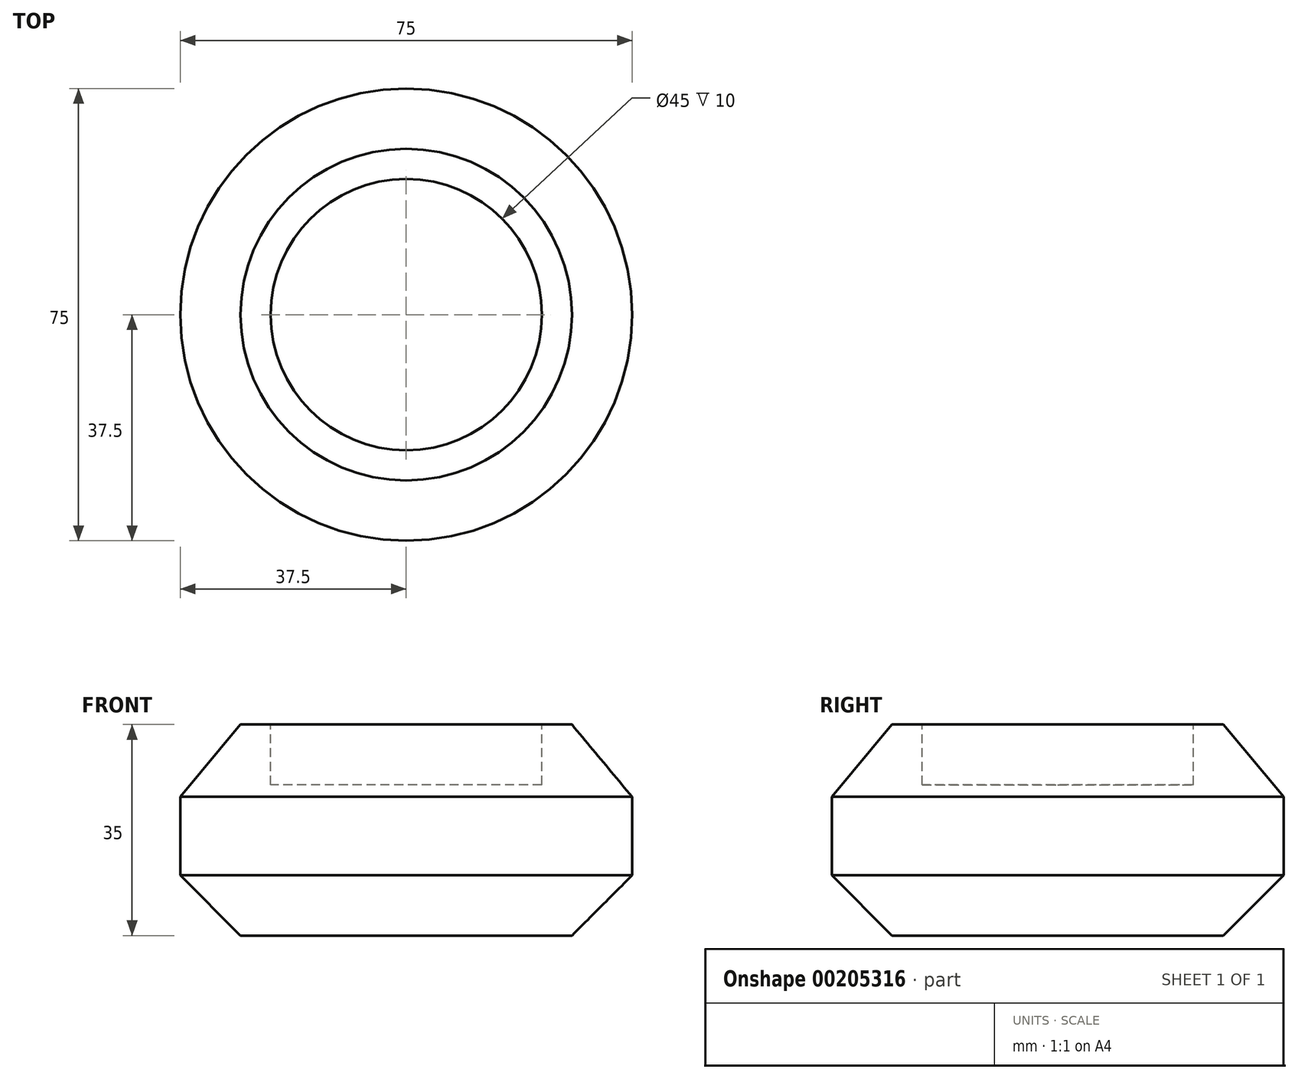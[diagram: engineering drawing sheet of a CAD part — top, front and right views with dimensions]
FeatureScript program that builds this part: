
annotation { "Feature Type Name" : "Feature", "Feature Type Description" : "" }
export const myFeature = defineFeature(function(context is Context, id is Id, definition is map)
    precondition{}
    {
        {
            var Q0;
            Q0=qCreatedBy(makeId("Top.planeOp"),FACE);
            var sketch = newSketch(context, id + "F0", { "sketchPlane" : qUnion([Q0])});
            skCircle(sketch, "E0", {"center": v(0, 0) * mm, "radius": 37.5 * mm});
            skSolve(sketch);
        }
        {
            var Q0;
            Q0=makeQuery(id+"F0.imprint","IMPRINT",FACE,{"disambiguationData":[TD([[makeQuery(id+"F0.imprint","IMPRINT",EDGE,{"derivedFrom":sQuery(id+"F0.wireOp",EDGE,"E0")}),1.0]])]});
            extrude(context, id + "F1", {"entities" : qUnion([Q0]), "depth" : 35 * mm});
        }
        {
            var Q0;
            Q0=makeQuery(id+"F1.opExtrude","CAP_FACE",FACE,{"disambiguationData":[OSD([sQuery(id+"F0.wireOp",EDGE,"E0")])],"isStart":false});
            chamfer(context, id + "F2", {"entities" : qUnion([Q0]), "chamferType" : ChamferType.TWO_OFFSETS, "width1" : 10 * mm, "oppositeDirection" : false, "width2" : 12 * mm, "tangentPropagation" : true});
        }
        {
            var Q0;
            Q0=makeQuery(id+"F1.opExtrude","CAP_FACE",FACE,{"disambiguationData":[OSD([sQuery(id+"F0.wireOp",EDGE,"E0")])],"isStart":false});
            var sketch = newSketch(context, id + "F3", { "sketchPlane" : qUnion([Q0])});
            skCircle(sketch, "E1", {"center": v(0, 0) * mm, "radius": 22.5 * mm});
            skSolve(sketch);
        }
        {
            var Q0;
            Q0=makeQuery(id+"F3.imprint","IMPRINT",FACE,{"disambiguationData":[TD([[makeQuery(id+"F3.imprint","IMPRINT",EDGE,{"derivedFrom":sQuery(id+"F3.wireOp",EDGE,"E1")}),1.0]])]});
            extrude(context, id + "F4", {"entities" : qUnion([Q0]), "operationType" : NewBodyOperationType.REMOVE, "oppositeDirection" : true, "depth" : 10 * mm});
        }
        {
            var Q0;
            Q0=makeQuery(id+"F4.boolean.opBoolean","COPY",EDGE,{"derivedFrom":makeQuery(id+"F4.opExtrude","CAP_EDGE",EDGE,{"disambiguationData":[OSD([sQuery(id+"F3.wireOp",EDGE,"E1")])],"isStart":true})});
            var Q1;
            Q1=makeQuery(id+"F1.opExtrude","CAP_EDGE",EDGE,{"disambiguationData":[OSD([sQuery(id+"F0.wireOp",EDGE,"E0")])],"isStart":true});
            chamfer(context, id + "F5", {"entities" : qUnion([Q0, Q1]), "width" : 10 * mm, "tangentPropagation" : true});
        }
    });
